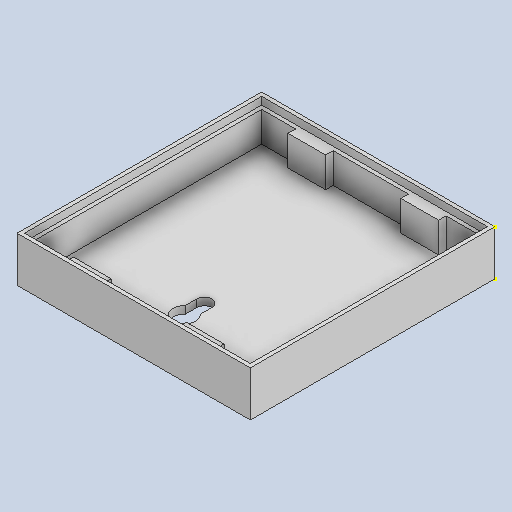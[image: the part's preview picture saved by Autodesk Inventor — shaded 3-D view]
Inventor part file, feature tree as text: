
AUTODESK INVENTOR PART (.ipt)
format: ipt  version: 2022 (Build 260153000, 153)  size: 168,960 bytes
history: native  units: in
note: dims shown in document units (in); Inventor stores cm internally (conversion verified against a paired STEP export)
features: sketch x7, other x2, shell x1
ambient origin geometry x8: Origin, YZ Plane, XZ Plane, XY Plane, X Axis, Y Axis, Z Axis, Center Point
bodies: Solid1 (feature_tree)
feature tree (10):
  shell  "Shell 1 bottom.ipt"  Thickness=0.3937in
  other  "Solid1::Shell 1 bottom.ipt"
  other  "TaggingFeature1"
  sketch  "Sketch1"
  sketch  "Sketch2"
  sketch  "Sketch3"
  sketch  "Sketch4"
  sketch  "Sketch10"
  sketch  "Sketch12"
  sketch  "Sketch13"
